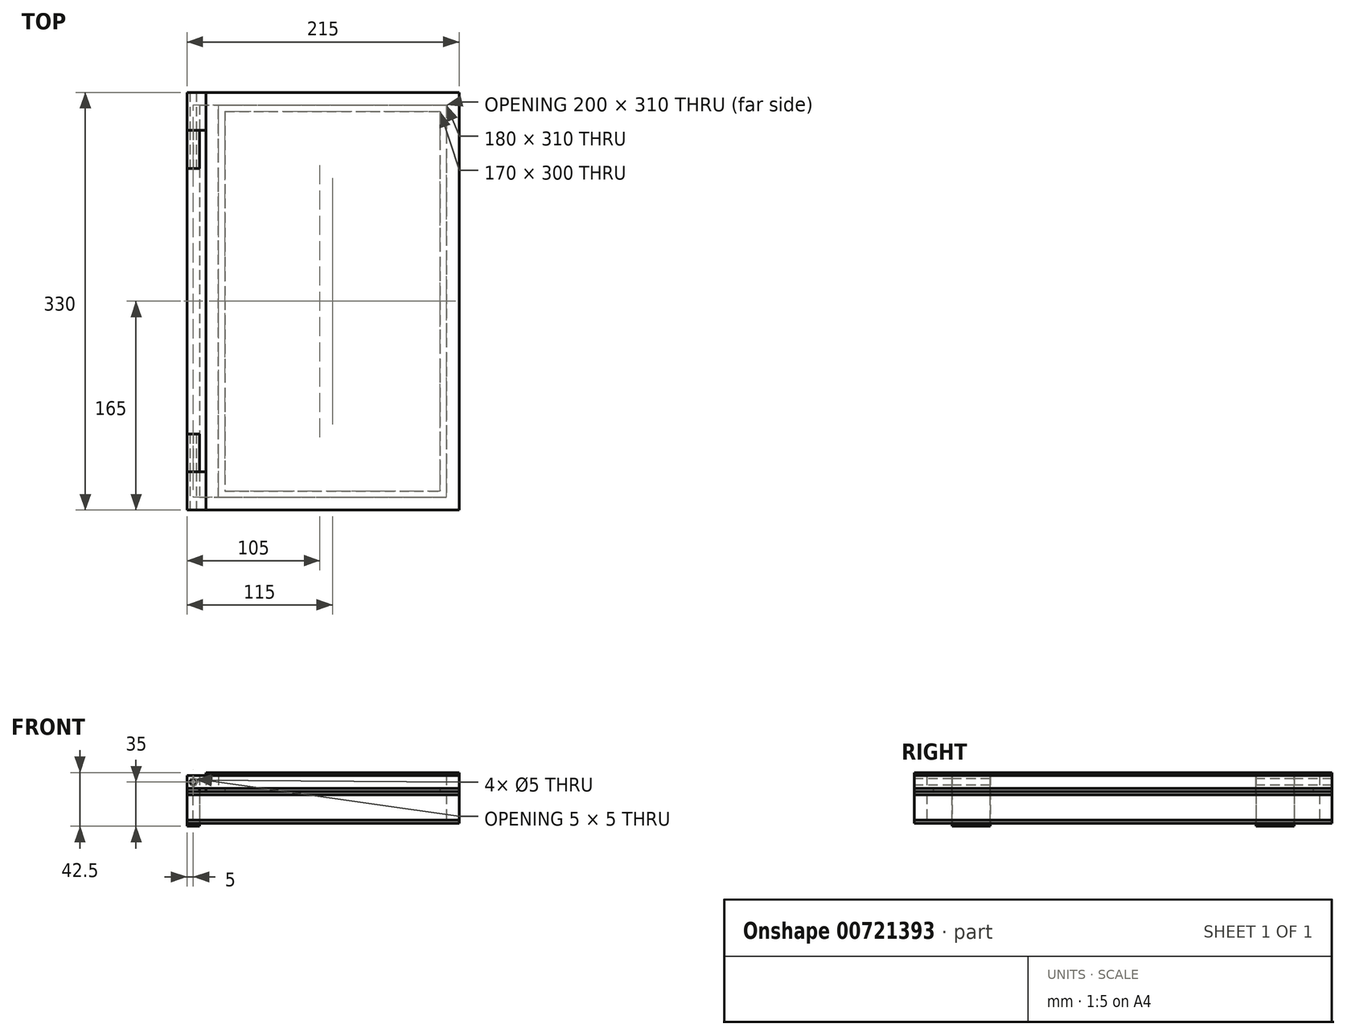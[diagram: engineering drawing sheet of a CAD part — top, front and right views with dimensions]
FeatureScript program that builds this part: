
annotation { "Feature Type Name" : "Feature", "Feature Type Description" : "" }
export const myFeature = defineFeature(function(context is Context, id is Id, definition is map)
    precondition{}
    {
        {
            var Q0;
            Q0=qCreatedBy(makeId("Top.planeOp"),FACE);
            var sketch = newSketch(context, id + "F0", { "sketchPlane" : qUnion([Q0])});
            skLineSegment(sketch, "E0.bottom", {"start": v(0, 0) * mm, "end": v(215, 0) * mm});
            skLineSegment(sketch, "E0.top", {"start": v(0, 330) * mm, "end": v(215, 330) * mm});
            skLineSegment(sketch, "E0.left", {"start": v(0, 0) * mm, "end": v(0, 330) * mm});
            skLineSegment(sketch, "E0.right", {"start": v(215, 0) * mm, "end": v(215, 330) * mm});
            skSolve(sketch);
        }
        {
            var Q0;
            Q0=makeQuery(id+"F0.imprint","IMPRINT",FACE,{"disambiguationData":[TD([[makeQuery(id+"F0.imprint","IMPRINT",EDGE,{"derivedFrom":sQuery(id+"F0.wireOp",EDGE,"E0.bottom")}),1.0]])]});
            extrude(context, id + "F1", {"entities" : qUnion([Q0]), "depth" : 2.5 * mm, "offsetDistance" : 25 * mm});
        }
        {
            var Q0;
            Q0=makeQuery(id+"F1.opExtrude","CAP_FACE",FACE,{"disambiguationData":[OSD([sQuery(id+"F0.wireOp",EDGE,"E0.bottom"),sQuery(id+"F0.wireOp",EDGE,"E0.top"),sQuery(id+"F0.wireOp",EDGE,"E0.left"),sQuery(id+"F0.wireOp",EDGE,"E0.right")])],"isStart":false});
            var sketch = newSketch(context, id + "F2", { "sketchPlane" : qUnion([Q0])});
            skLineSegment(sketch, "E1", {"start": v(215, 0) * mm, "end": v(215, 10) * mm, "construction": true});
            skLineSegment(sketch, "E2", {"start": v(215, 10) * mm, "end": v(205, 10) * mm, "construction": true});
            skLineSegment(sketch, "E3", {"start": v(0, 330) * mm, "end": v(0, 320) * mm, "construction": true});
            skLineSegment(sketch, "E4", {"start": v(0, 320) * mm, "end": v(10, 320) * mm, "construction": true});
            skLineSegment(sketch, "E5.bottom", {"start": v(10, 320) * mm, "end": v(205, 320) * mm});
            skLineSegment(sketch, "E5.top", {"start": v(10, 10) * mm, "end": v(205, 10) * mm});
            skLineSegment(sketch, "E5.left", {"start": v(10, 320) * mm, "end": v(10, 10) * mm});
            skLineSegment(sketch, "E5.right", {"start": v(205, 320) * mm, "end": v(205, 10) * mm});
            skLineSegment(sketch, "E6.bottom", {"start": v(0, 0) * mm, "end": v(215, 0) * mm});
            skLineSegment(sketch, "E6.top", {"start": v(0, 330) * mm, "end": v(215, 330) * mm});
            skLineSegment(sketch, "E6.left", {"start": v(0, 0) * mm, "end": v(0, 330) * mm});
            skLineSegment(sketch, "E6.right", {"start": v(215, 0) * mm, "end": v(215, 330) * mm});
            skSolve(sketch);
        }
        {
            var Q0;
            Q0=qSketchRegion(id+"F2",true);
            extrude(context, id + "F3", {"entities" : qUnion([Q0]), "depth" : 20 * mm, "offsetDistance" : 25 * mm});
        }
        {
            var Q0;
            Q0=qCreatedBy(makeId("Front.planeOp"),FACE);
            var sketch = newSketch(context, id + "F4", { "sketchPlane" : qUnion([Q0])});
            skLineSegment(sketch, "E7", {"start": v(0, 0) * mm, "end": v(0, 2.5) * mm});
            skLineSegment(sketch, "E8", {"start": v(0, 2.5) * mm, "end": v(5, 2.5) * mm});
            skLineSegment(sketch, "E9", {"start": v(5, 2.5) * mm, "end": v(5, 22.5) * mm});
            skLineSegment(sketch, "E10", {"start": v(5, 22.5) * mm, "end": v(0, 22.5) * mm});
            skLineSegment(sketch, "E11", {"start": v(0, 22.5) * mm, "end": v(0, 37.5) * mm});
            skLineSegment(sketch, "E12", {"start": v(0, 37.5) * mm, "end": v(10, 37.5) * mm});
            skLineSegment(sketch, "E13", {"start": v(10, 37.5) * mm, "end": v(10, -2.5) * mm});
            skLineSegment(sketch, "E14", {"start": v(10, -2.5) * mm, "end": v(0, -2.5) * mm});
            skLineSegment(sketch, "E15", {"start": v(0, -2.5) * mm, "end": v(0, 0) * mm});
            skLineSegment(sketch, "E16", {"start": v(5, 37.5) * mm, "end": v(5, 32.5) * mm, "construction": true});
            skCircle(sketch, "E17", {"center": v(5, 32.5) * mm, "radius": 2.5 * mm});
            skSolve(sketch);
        }
        {
            var Q0;
            Q0=qSketchRegion(id+"F4",true);
            extrude(context, id + "F5", {"entities" : qUnion([Q0]), "oppositeDirection" : true, "depth" : 30 * mm, "offsetDistance" : 25 * mm});
        }
        {
            var Q0;
            Q0=makeQuery(id+"F5.opExtrude","SWEPT_BODY",BODY,{"disambiguationData":[OSD([sQuery(id+"F4.wireOp",EDGE,"E7"),sQuery(id+"F4.wireOp",EDGE,"E8"),sQuery(id+"F4.wireOp",EDGE,"E9"),sQuery(id+"F4.wireOp",EDGE,"E10"),sQuery(id+"F4.wireOp",EDGE,"E11"),sQuery(id+"F4.wireOp",EDGE,"E12"),sQuery(id+"F4.wireOp",EDGE,"E13"),sQuery(id+"F4.wireOp",EDGE,"E14"),sQuery(id+"F4.wireOp",EDGE,"E15"),sQuery(id+"F4.wireOp",EDGE,"E17")])]});
            transform(context, id + "F6", {"entities" : qUnion([Q0]), "transformType" : TransformType.TRANSLATION_3D, "dx" : 0 * mm, "dy" : 30 * mm, "dz" : 0 * mm, "makeCopy" : false});
        }
        {
            var Q0;
            Q0=makeQuery(id+"F5.opExtrude","SWEPT_BODY",BODY,{"disambiguationData":[OSD([sQuery(id+"F4.wireOp",EDGE,"E7"),sQuery(id+"F4.wireOp",EDGE,"E8"),sQuery(id+"F4.wireOp",EDGE,"E9"),sQuery(id+"F4.wireOp",EDGE,"E10"),sQuery(id+"F4.wireOp",EDGE,"E11"),sQuery(id+"F4.wireOp",EDGE,"E12"),sQuery(id+"F4.wireOp",EDGE,"E13"),sQuery(id+"F4.wireOp",EDGE,"E14"),sQuery(id+"F4.wireOp",EDGE,"E15"),sQuery(id+"F4.wireOp",EDGE,"E17")])]});
            transform(context, id + "F7", {"entities" : qUnion([Q0]), "transformType" : TransformType.TRANSLATION_3D, "dx" : 0 * mm, "dy" : 240 * mm, "dz" : 0 * mm, "makeCopy" : true});
        }
        {
            var Q0;
            Q0=makeQuery(id+"F3.opExtrude","CAP_FACE",FACE,{"disambiguationData":[OSD([sQuery(id+"F2.wireOp",EDGE,"E5.bottom"),sQuery(id+"F2.wireOp",EDGE,"E5.top"),sQuery(id+"F2.wireOp",EDGE,"E5.left"),sQuery(id+"F2.wireOp",EDGE,"E5.right"),sQuery(id+"F2.wireOp",EDGE,"E6.bottom"),sQuery(id+"F2.wireOp",EDGE,"E6.top"),sQuery(id+"F2.wireOp",EDGE,"E6.left"),sQuery(id+"F2.wireOp",EDGE,"E6.right")])],"isStart":false});
            var sketch = newSketch(context, id + "F8", { "sketchPlane" : qUnion([Q0])});
            skLineSegment(sketch, "E18.bottom", {"start": v(0, 0) * mm, "end": v(215, 0) * mm});
            skLineSegment(sketch, "E18.top", {"start": v(0, 330) * mm, "end": v(215, 330) * mm});
            skLineSegment(sketch, "E18.left", {"start": v(0, 0) * mm, "end": v(0, 330) * mm});
            skLineSegment(sketch, "E18.right", {"start": v(215, 0) * mm, "end": v(215, 330) * mm});
            skSolve(sketch);
        }
        {
            var Q0;
            Q0=qSketchRegion(id+"F8",true);
            extrude(context, id + "F9", {"entities" : qUnion([Q0]), "depth" : 2.5 * mm, "offsetDistance" : 25 * mm});
        }
        {
            var Q0;
            Q0=makeQuery(id+"F7.opPattern","COPY",BODY,{"derivedFrom":makeQuery(id+"F5.opExtrude","SWEPT_BODY",BODY,{"disambiguationData":[OSD([sQuery(id+"F4.wireOp",EDGE,"E7"),sQuery(id+"F4.wireOp",EDGE,"E8"),sQuery(id+"F4.wireOp",EDGE,"E9"),sQuery(id+"F4.wireOp",EDGE,"E10"),sQuery(id+"F4.wireOp",EDGE,"E11"),sQuery(id+"F4.wireOp",EDGE,"E12"),sQuery(id+"F4.wireOp",EDGE,"E13"),sQuery(id+"F4.wireOp",EDGE,"E14"),sQuery(id+"F4.wireOp",EDGE,"E15"),sQuery(id+"F4.wireOp",EDGE,"E17")])]}),"instanceName":"1"});
            var Q1;
            Q1=makeQuery(id+"F5.opExtrude","SWEPT_BODY",BODY,{"disambiguationData":[OSD([sQuery(id+"F4.wireOp",EDGE,"E7"),sQuery(id+"F4.wireOp",EDGE,"E8"),sQuery(id+"F4.wireOp",EDGE,"E9"),sQuery(id+"F4.wireOp",EDGE,"E10"),sQuery(id+"F4.wireOp",EDGE,"E11"),sQuery(id+"F4.wireOp",EDGE,"E12"),sQuery(id+"F4.wireOp",EDGE,"E13"),sQuery(id+"F4.wireOp",EDGE,"E14"),sQuery(id+"F4.wireOp",EDGE,"E15"),sQuery(id+"F4.wireOp",EDGE,"E17")])]});
            var Q2;
            Q2=makeQuery(id+"F3.opExtrude","SWEPT_BODY",BODY,{"disambiguationData":[OSD([sQuery(id+"F2.wireOp",EDGE,"E5.bottom"),sQuery(id+"F2.wireOp",EDGE,"E5.top"),sQuery(id+"F2.wireOp",EDGE,"E5.left"),sQuery(id+"F2.wireOp",EDGE,"E5.right"),sQuery(id+"F2.wireOp",EDGE,"E6.bottom"),sQuery(id+"F2.wireOp",EDGE,"E6.top"),sQuery(id+"F2.wireOp",EDGE,"E6.left"),sQuery(id+"F2.wireOp",EDGE,"E6.right")])]});
            var Q3;
            Q3=makeQuery(id+"F9.opExtrude","SWEPT_BODY",BODY,{"disambiguationData":[OSD([sQuery(id+"F8.wireOp",EDGE,"E18.bottom"),sQuery(id+"F8.wireOp",EDGE,"E18.top"),sQuery(id+"F8.wireOp",EDGE,"E18.left"),sQuery(id+"F8.wireOp",EDGE,"E18.right")])]});
            var Q4;
            Q4=makeQuery(id+"F1.opExtrude","SWEPT_BODY",BODY,{"disambiguationData":[OSD([sQuery(id+"F0.wireOp",EDGE,"E0.bottom"),sQuery(id+"F0.wireOp",EDGE,"E0.top"),sQuery(id+"F0.wireOp",EDGE,"E0.left"),sQuery(id+"F0.wireOp",EDGE,"E0.right")])]});
            booleanBodies(context, id + "F10", {"operationType" : BooleanOperationType.SUBTRACTION, "tools" : qUnion([Q0, Q1]), "targets" : qUnion([Q2, Q3, Q4]), "keepTools" : true});
        }
        {
            var Q0;
            Q0=makeQuery(id+"F9.opExtrude","CAP_FACE",FACE,{"disambiguationData":[OSD([sQuery(id+"F8.wireOp",EDGE,"E18.bottom"),sQuery(id+"F8.wireOp",EDGE,"E18.top"),sQuery(id+"F8.wireOp",EDGE,"E18.left"),sQuery(id+"F8.wireOp",EDGE,"E18.right")])],"isStart":false});
            var sketch = newSketch(context, id + "F11", { "sketchPlane" : qUnion([Q0])});
            skLineSegment(sketch, "E19.bottom", {"start": v(215, 0) * mm, "end": v(15, 0) * mm});
            skLineSegment(sketch, "E19.top", {"start": v(215, 330) * mm, "end": v(15, 330) * mm});
            skLineSegment(sketch, "E19.left", {"start": v(215, 0) * mm, "end": v(215, 330) * mm});
            skLineSegment(sketch, "E19.right", {"start": v(15, 0) * mm, "end": v(15, 330) * mm});
            skLineSegment(sketch, "E20", {"start": v(215, 0) * mm, "end": v(215, 15) * mm, "construction": true});
            skLineSegment(sketch, "E21", {"start": v(215, 15) * mm, "end": v(200, 15) * mm, "construction": true});
            skLineSegment(sketch, "E22", {"start": v(15, 330) * mm, "end": v(15, 315) * mm, "construction": true});
            skLineSegment(sketch, "E23", {"start": v(15, 315) * mm, "end": v(30, 315) * mm, "construction": true});
            skLineSegment(sketch, "E24.bottom", {"start": v(30, 315) * mm, "end": v(200, 315) * mm});
            skLineSegment(sketch, "E24.top", {"start": v(30, 15) * mm, "end": v(200, 15) * mm});
            skLineSegment(sketch, "E24.left", {"start": v(30, 315) * mm, "end": v(30, 15) * mm});
            skLineSegment(sketch, "E24.right", {"start": v(200, 315) * mm, "end": v(200, 15) * mm});
            skSolve(sketch);
        }
        {
            var Q0;
            Q0=qSketchRegion(id+"F11",true);
            extrude(context, id + "F12", {"entities" : qUnion([Q0]), "depth" : 2.5 * mm, "offsetDistance" : 25 * mm});
        }
        {
            var Q0;
            Q0=makeQuery(id+"F12.opExtrude","CAP_FACE",FACE,{"disambiguationData":[OSD([sQuery(id+"F11.wireOp",EDGE,"E19.bottom"),sQuery(id+"F11.wireOp",EDGE,"E19.top"),sQuery(id+"F11.wireOp",EDGE,"E19.left"),sQuery(id+"F11.wireOp",EDGE,"E19.right"),sQuery(id+"F11.wireOp",EDGE,"E24.bottom"),sQuery(id+"F11.wireOp",EDGE,"E24.top"),sQuery(id+"F11.wireOp",EDGE,"E24.left"),sQuery(id+"F11.wireOp",EDGE,"E24.right")])],"isStart":false});
            var sketch = newSketch(context, id + "F13", { "sketchPlane" : qUnion([Q0])});
            skLineSegment(sketch, "E25.bottom", {"start": v(215, 0) * mm, "end": v(0, 0) * mm});
            skLineSegment(sketch, "E25.top", {"start": v(215, 330) * mm, "end": v(0, 330) * mm});
            skLineSegment(sketch, "E25.left", {"start": v(215, 0) * mm, "end": v(215, 330) * mm});
            skLineSegment(sketch, "E25.right", {"start": v(0, 0) * mm, "end": v(0, 330) * mm, "construction": true});
            skLineSegment(sketch, "E26", {"start": v(0, 0) * mm, "end": v(0, 30) * mm});
            skLineSegment(sketch, "E27", {"start": v(0, 30) * mm, "end": v(15, 30) * mm});
            skLineSegment(sketch, "E28", {"start": v(0, 330) * mm, "end": v(0, 300) * mm});
            skLineSegment(sketch, "E29", {"start": v(0, 300) * mm, "end": v(15, 300) * mm});
            skLineSegment(sketch, "E30", {"start": v(15, 300) * mm, "end": v(15, 30) * mm});
            skLineSegment(sketch, "E31", {"start": v(215, 330) * mm, "end": v(215, 320) * mm, "construction": true});
            skLineSegment(sketch, "E32", {"start": v(215, 320) * mm, "end": v(205, 320) * mm, "construction": true});
            skLineSegment(sketch, "E33", {"start": v(15, 30) * mm, "end": v(25, 30) * mm, "construction": true});
            skLineSegment(sketch, "E34", {"start": v(25, 30) * mm, "end": v(25, 10) * mm, "construction": true});
            skLineSegment(sketch, "E35.bottom", {"start": v(25, 10) * mm, "end": v(205, 10) * mm});
            skLineSegment(sketch, "E35.top", {"start": v(25, 320) * mm, "end": v(205, 320) * mm});
            skLineSegment(sketch, "E35.left", {"start": v(25, 10) * mm, "end": v(25, 320) * mm});
            skLineSegment(sketch, "E35.right", {"start": v(205, 10) * mm, "end": v(205, 320) * mm});
            skSolve(sketch);
        }
        {
            var Q0;
            Q0=qSketchRegion(id+"F13",true);
            extrude(context, id + "F14", {"entities" : qUnion([Q0]), "depth" : 10 * mm, "offsetDistance" : 25 * mm});
        }
        {
            var Q0;
            Q0=makeQuery(id+"F14.opExtrude","CAP_FACE",FACE,{"disambiguationData":[OSD([sQuery(id+"F13.wireOp",EDGE,"E25.bottom"),sQuery(id+"F13.wireOp",EDGE,"E25.top"),sQuery(id+"F13.wireOp",EDGE,"E25.left"),sQuery(id+"F13.wireOp",EDGE,"E26"),sQuery(id+"F13.wireOp",EDGE,"E27"),sQuery(id+"F13.wireOp",EDGE,"E28"),sQuery(id+"F13.wireOp",EDGE,"E29"),sQuery(id+"F13.wireOp",EDGE,"E30"),sQuery(id+"F13.wireOp",EDGE,"E35.bottom"),sQuery(id+"F13.wireOp",EDGE,"E35.top"),sQuery(id+"F13.wireOp",EDGE,"E35.left"),sQuery(id+"F13.wireOp",EDGE,"E35.right")])],"isStart":false});
            var sketch = newSketch(context, id + "F15", { "sketchPlane" : qUnion([Q0])});
            skLineSegment(sketch, "E36.bottom", {"start": v(215, 0) * mm, "end": v(15, 0) * mm});
            skLineSegment(sketch, "E36.top", {"start": v(215, 330) * mm, "end": v(15, 330) * mm});
            skLineSegment(sketch, "E36.left", {"start": v(215, 0) * mm, "end": v(215, 330) * mm});
            skLineSegment(sketch, "E36.right", {"start": v(15, 0) * mm, "end": v(15, 330) * mm});
            skSolve(sketch);
        }
        {
            var Q0;
            Q0=qSketchRegion(id+"F15",true);
            extrude(context, id + "F16", {"entities" : qUnion([Q0]), "depth" : 2.5 * mm, "offsetDistance" : 25 * mm});
        }
        {
            var Q0;
            Q0=makeQuery(id+"F14.opExtrude","SWEPT_FACE",FACE,{"disambiguationData":[OSD([sQuery(id+"F13.wireOp",EDGE,"E25.bottom")])]});
            var sketch = newSketch(context, id + "F17", { "sketchPlane" : qUnion([Q0])});
            skLineSegment(sketch, "E37", {"start": v(0, 32.5) * mm, "end": v(5, 32.5) * mm, "construction": true});
            skCircle(sketch, "E38", {"center": v(5, 32.5) * mm, "radius": 2.5 * mm});
            skSolve(sketch);
        }
        {
            var Q0;
            Q0=qSketchRegion(id+"F17",true);
            extrude(context, id + "F18", {"entities" : qUnion([Q0]), "operationType" : NewBodyOperationType.REMOVE, "oppositeDirection" : true, "depth" : 999 * mm, "offsetDistance" : 25 * mm});
        }
    });
